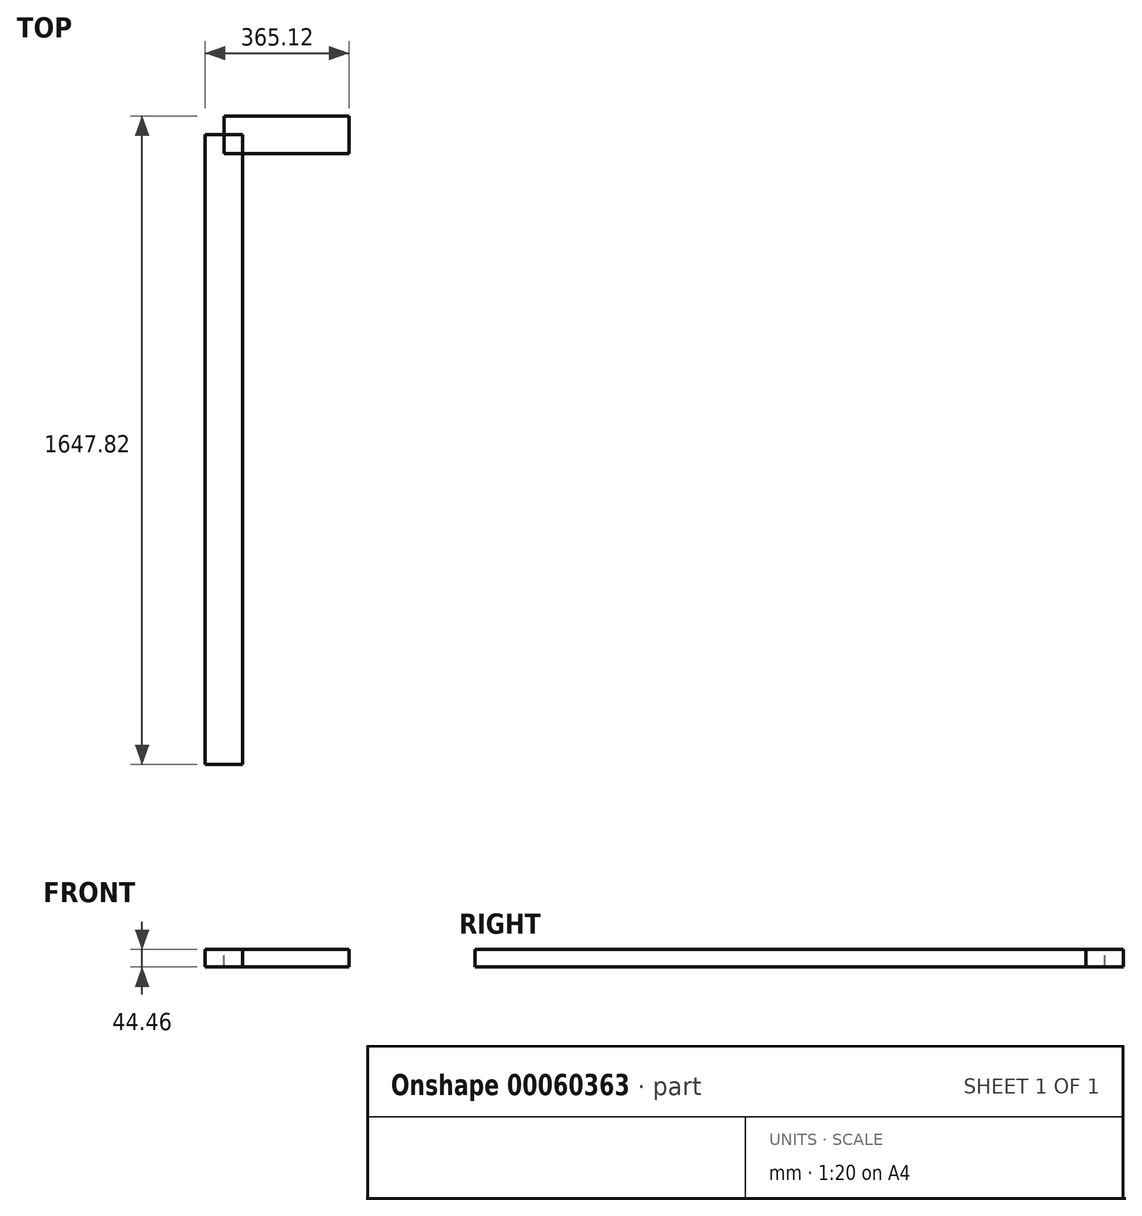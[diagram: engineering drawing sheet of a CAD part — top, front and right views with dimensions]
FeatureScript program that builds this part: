
annotation { "Feature Type Name" : "Feature", "Feature Type Description" : "" }
export const myFeature = defineFeature(function(context is Context, id is Id, definition is map)
    precondition{}
    {
        {
            var Q0;
            Q0=qCreatedBy(makeId("Front.planeOp"),FACE);
            var sketch = newSketch(context, id + "F0", { "sketchPlane" : qUnion([Q0])});
            skLineSegment(sketch, "E0.rect.bottom", {"start": v(47.62, -22.22) * mm, "end": v(-47.62, -22.23) * mm});
            skLineSegment(sketch, "E0.rect.top", {"start": v(47.62, 22.23) * mm, "end": v(-47.63, 22.22) * mm});
            skLineSegment(sketch, "E0.rect.left", {"start": v(47.62, -22.22) * mm, "end": v(47.62, 22.23) * mm});
            skLineSegment(sketch, "E0.rect.right", {"start": v(-47.63, -22.23) * mm, "end": v(-47.63, 22.23) * mm});
            skPoint(sketch, "E0.rect.middle", {"position": v(0, 0) * mm});
            skSolve(sketch);
        }
        {
            var Q0;
            Q0=makeQuery(id+"F0.imprint","IMPRINT",FACE,{"disambiguationData":[TD([[makeQuery(id+"F0.imprint","IMPRINT",EDGE,{"derivedFrom":sQuery(id+"F0.wireOp",EDGE,"E0.rect.bottom")}),-1.0]])]});
            extrude(context, id + "F1", {"entities" : qUnion([Q0]), "depth" : 1600.2 * mm});
        }
        {
            var Q0;
            Q0=qCreatedBy(makeId("Right.planeOp"),FACE);
            var sketch = newSketch(context, id + "F2", { "sketchPlane" : qUnion([Q0])});
            skLineSegment(sketch, "E1.rect.bottom", {"start": v(-47.62, -22.22) * mm, "end": v(47.63, -22.22) * mm});
            skLineSegment(sketch, "E1.rect.top", {"start": v(-47.63, 22.22) * mm, "end": v(47.62, 22.22) * mm});
            skLineSegment(sketch, "E1.rect.left", {"start": v(-47.62, -22.22) * mm, "end": v(-47.63, 22.22) * mm});
            skLineSegment(sketch, "E1.rect.right", {"start": v(47.63, -22.22) * mm, "end": v(47.62, 22.22) * mm});
            skPoint(sketch, "E1.rect.middle", {"position": v(0, 0) * mm});
            skSolve(sketch);
        }
        {
            var Q0;
            Q0=makeQuery(id+"F2.imprint","IMPRINT",FACE,{"disambiguationData":[TD([[makeQuery(id+"F2.imprint","IMPRINT",EDGE,{"derivedFrom":sQuery(id+"F2.wireOp",EDGE,"E1.rect.bottom")}),1.0]])]});
            extrude(context, id + "F3", {"entities" : qUnion([Q0]), "depth" : 317.5 * mm});
        }
    });
